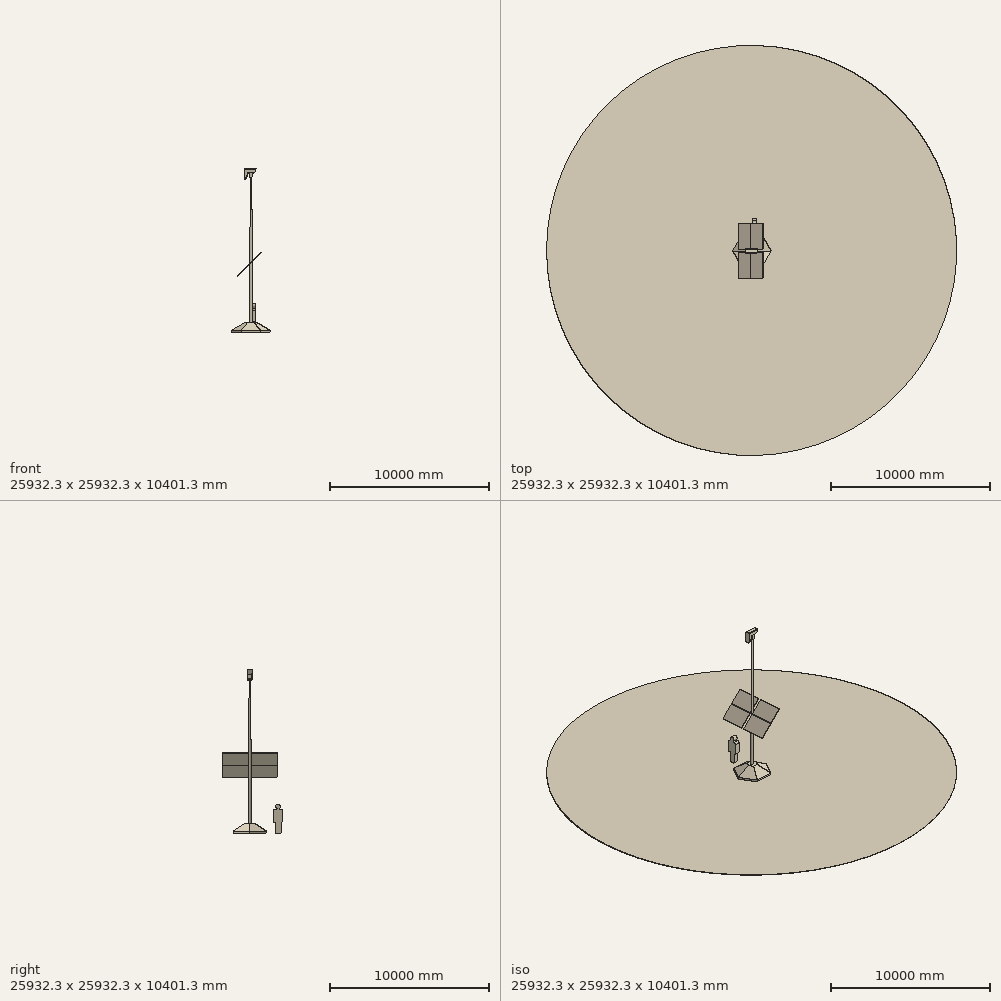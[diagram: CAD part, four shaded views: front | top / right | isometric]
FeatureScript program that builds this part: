
annotation { "Feature Type Name" : "Feature", "Feature Type Description" : "" }
export const myFeature = defineFeature(function(context is Context, id is Id, definition is map)
    precondition{}
    {
        {
            var Q0;
            Q0=qCreatedBy(makeId("Top.planeOp"),FACE);
            var sketch = newSketch(context, id + "F0", { "sketchPlane" : qUnion([Q0])});
            skCircle(sketch, "E0", {"center": v(0, 0) * mm, "radius": 101.6 * mm});
            skSolve(sketch);
        }
        {
            var Q0;
            Q0=qCreatedBy(makeId("Top.planeOp"),FACE);
            cPlane(context, id + "F1", {"entities" : qUnion([Q0]), "cplaneType" : CPlaneType.OFFSET, "offset" : 9144 * mm, "width" : 152.4 * mm, "height" : 152.4 * mm});
        }
        {
            var Q0;
            Q0=qCreatedBy(id+"F1.planeOp",FACE);
            var sketch = newSketch(context, id + "F2", { "sketchPlane" : qUnion([Q0])});
            skCircle(sketch, "E1", {"center": v(0, 0) * mm, "radius": 48.26 * mm});
            skSolve(sketch);
        }
        {
            var Q0;
            Q0=makeQuery(id+"F0.imprint","IMPRINT",FACE,{"disambiguationData":[TD([[makeQuery(id+"F0.imprint","IMPRINT",EDGE,{"derivedFrom":sQuery(id+"F0.wireOp",EDGE,"E0")}),1.0]])]});
            var Q1;
            Q1=makeQuery(id+"F2.imprint","IMPRINT",FACE,{"disambiguationData":[TD([[makeQuery(id+"F2.imprint","IMPRINT",EDGE,{"derivedFrom":sQuery(id+"F2.wireOp",EDGE,"E1")}),1.0]])]});
            loft(context, id + "F3", {"sheetProfilesArray" : [{ "sheetProfileEntities" : qUnion([Q0]) }, { "sheetProfileEntities" : qUnion([Q1]) }]});
        }
        {
            var Q0;
            Q0=qCreatedBy(makeId("Front.planeOp"),FACE);
            var sketch = newSketch(context, id + "F4", { "sketchPlane" : qUnion([Q0])});
            skLineSegment(sketch, "E2", {"start": v(703.54, 4411.94) * mm, "end": v(-50.8, 3657.6) * mm});
            skLineSegment(sketch, "E3", {"start": v(-50.8, 3657.6) * mm, "end": v(-86.72, 3693.52) * mm});
            skLineSegment(sketch, "E4", {"start": v(-86.72, 3693.52) * mm, "end": v(667.62, 4447.86) * mm});
            skLineSegment(sketch, "E5", {"start": v(667.62, 4447.86) * mm, "end": v(703.54, 4411.94) * mm});
            skLineSegment(sketch, "E6", {"start": v(-50.8, 3657.6) * mm, "end": v(703.54, 3657.6) * mm});
            skSolve(sketch);
        }
        {
            var Q0;
            Q0 = qSketchRegion(id + "F4", true);
            extrude(context, id + "F5", {"entities" : qUnion([Q0]), "depth" : 1752.6 * mm, "offsetDistance" : 25.4 * mm, "hasSecondDirection" : true, "secondDirectionOppositeDirection" : true, "secondDirectionDepth" : -101.6 * mm});
        }
        {
            var Q0;
            Q0=makeQuery(id+"F3.opLoft","CAP_FACE",FACE,{"disambiguationData":[OSD([makeQuery(id+"F2.imprint","IMPRINT",FACE,{"disambiguationData":[TD([[makeQuery(id+"F2.imprint","IMPRINT",EDGE,{"derivedFrom":sQuery(id+"F2.wireOp",EDGE,"E1")}),1.0]])]})])],"isStart":true});
            var Q1;
            Q1=makeQuery(id+"F3.opLoft","CAP_FACE",FACE,{"disambiguationData":[OSD([makeQuery(id+"F0.imprint","IMPRINT",FACE,{"disambiguationData":[TD([[makeQuery(id+"F0.imprint","IMPRINT",EDGE,{"derivedFrom":sQuery(id+"F0.wireOp",EDGE,"E0")}),1.0]])]})])],"isStart":true});
            shell(context, id + "F6", {"entities" : qUnion([Q0, Q1]), "thickness" : 4.13 * mm});
        }
        {
            var Q0;
            Q0=makeQuery(id+"F5.opExtrude","SWEPT_BODY",BODY,{"disambiguationData":[OSD([sQuery(id+"F4.wireOp",EDGE,"E2"),sQuery(id+"F4.wireOp",EDGE,"E3"),sQuery(id+"F4.wireOp",EDGE,"E4"),sQuery(id+"F4.wireOp",EDGE,"E5")])]});
            var Q1;
            Q1=qCreatedBy(makeId("Front.planeOp"),FACE);
            mirror(context, id + "F7", {"entities" : qUnion([Q0]), "mirrorPlane" : qUnion([Q1])});
        }
        {
            var Q0;
            Q0=makeQuery(id+"F5.opExtrude","SWEPT_FACE",FACE,{"disambiguationData":[OSD([sQuery(id+"F4.wireOp",EDGE,"E3")])]});
            cPlane(context, id + "F8", {"entities" : qUnion([Q0]), "cplaneType" : CPlaneType.OFFSET, "offset" : 12.7 * mm, "width" : 152.4 * mm, "height" : 152.4 * mm});
        }
        {
            var Q0;
            Q0=makeQuery(id+"F5.opExtrude","SWEPT_BODY",BODY,{"disambiguationData":[OSD([sQuery(id+"F4.wireOp",EDGE,"E2"),sQuery(id+"F4.wireOp",EDGE,"E3"),sQuery(id+"F4.wireOp",EDGE,"E4"),sQuery(id+"F4.wireOp",EDGE,"E5")])]});
            var Q1;
            Q1=makeQuery(id+"F7.opPattern","COPY",BODY,{"derivedFrom":makeQuery(id+"F5.opExtrude","SWEPT_BODY",BODY,{"disambiguationData":[OSD([sQuery(id+"F4.wireOp",EDGE,"E2"),sQuery(id+"F4.wireOp",EDGE,"E3"),sQuery(id+"F4.wireOp",EDGE,"E4"),sQuery(id+"F4.wireOp",EDGE,"E5")])]}),"instanceName":"1"});
            var Q2;
            Q2=qCreatedBy(id+"F8.planeOp",FACE);
            mirror(context, id + "F9", {"entities" : qUnion([Q0, Q1]), "mirrorPlane" : qUnion([Q2])});
        }
        {
            var Q0;
            Q0=makeQuery(id+"F3.opLoft","CAP_FACE",FACE,{"disambiguationData":[OSD([makeQuery(id+"F0.imprint","IMPRINT",FACE,{"disambiguationData":[TD([[makeQuery(id+"F0.imprint","IMPRINT",EDGE,{"derivedFrom":sQuery(id+"F0.wireOp",EDGE,"E0")}),1.0]])]})])],"isStart":true});
            var sketch = newSketch(context, id + "F10", { "sketchPlane" : qUnion([Q0])});
            skCircle(sketch, "E7.cCircle", {"center": v(0, 0) * mm, "radius": 1219.2 * mm, "construction": true});
            skLineSegment(sketch, "E7.0", {"start": v(1219.2, 0) * mm, "end": v(609.6, -1055.86) * mm});
            skLineSegment(sketch, "E7.1", {"start": v(609.6, -1055.86) * mm, "end": v(-609.6, -1055.86) * mm});
            skLineSegment(sketch, "E7.2", {"start": v(-609.6, -1055.86) * mm, "end": v(-1219.2, 0) * mm});
            skLineSegment(sketch, "E7.3", {"start": v(-1219.2, 0) * mm, "end": v(-609.6, 1055.86) * mm});
            skLineSegment(sketch, "E7.4", {"start": v(-609.6, 1055.86) * mm, "end": v(609.6, 1055.86) * mm});
            skLineSegment(sketch, "E7.5", {"start": v(609.6, 1055.86) * mm, "end": v(1219.2, 0) * mm});
            skSolve(sketch);
        }
        {
            var Q0;
            Q0 = qSketchRegion(id + "F10", true);
            extrude(context, id + "F11", {"entities" : qUnion([Q0]), "depth" : 635 * mm, "offsetDistance" : 25.4 * mm});
        }
        {
            var Q0;
            Q0=makeQuery(id+"F3.opLoft","CAP_FACE",FACE,{"disambiguationData":[OSD([makeQuery(id+"F2.imprint","IMPRINT",FACE,{"disambiguationData":[TD([[makeQuery(id+"F2.imprint","IMPRINT",EDGE,{"derivedFrom":sQuery(id+"F2.wireOp",EDGE,"E1")}),1.0]])]})])],"isStart":true});
            var sketch = newSketch(context, id + "F12", { "sketchPlane" : qUnion([Q0])});
            skLineSegment(sketch, "E8.bottom", {"start": v(76.2, 127) * mm, "end": v(-76.2, 127) * mm});
            skLineSegment(sketch, "E8.top", {"start": v(76.2, -127) * mm, "end": v(-76.2, -127) * mm});
            skLineSegment(sketch, "E8.left", {"start": v(76.2, 127) * mm, "end": v(76.2, -127) * mm});
            skLineSegment(sketch, "E8.right", {"start": v(-76.2, 127) * mm, "end": v(-76.2, -127) * mm});
            skPoint(sketch, "E8.middle", {"position": v(0, 0) * mm});
            skSolve(sketch);
        }
        {
            var Q0;
            Q0 = qSketchRegion(id + "F12", true);
            extrude(context, id + "F13", {"entities" : qUnion([Q0]), "operationType" : NewBodyOperationType.ADD, "depth" : 292.1 * mm, "offsetDistance" : 25.4 * mm});
        }
        {
            var Q0;
            Q0=qCreatedBy(makeId("Front.planeOp"),FACE);
            var sketch = newSketch(context, id + "F14", { "sketchPlane" : qUnion([Q0])});
            skLineSegment(sketch, "E9.0", {"start": v(76.2, 9436.1) * mm, "end": v(-76.2, 9436.1) * mm});
            skLineSegment(sketch, "E10", {"start": v(76.2, 9436.1) * mm, "end": v(228.6, 9436.1) * mm});
            skLineSegment(sketch, "E11", {"start": v(228.6, 9436.1) * mm, "end": v(348.34, 9740.9) * mm});
            skLineSegment(sketch, "E12", {"start": v(348.34, 9740.9) * mm, "end": v(-413.66, 9740.9) * mm});
            skLineSegment(sketch, "E13", {"start": v(-413.66, 9740.9) * mm, "end": v(-413.66, 9029.7) * mm});
            skLineSegment(sketch, "E14", {"start": v(-413.66, 9029.7) * mm, "end": v(-312.06, 9029.7) * mm});
            skLineSegment(sketch, "E15", {"start": v(-312.06, 9029.7) * mm, "end": v(-152.4, 9436.1) * mm});
            skLineSegment(sketch, "E16", {"start": v(-152.4, 9436.1) * mm, "end": v(-76.2, 9436.1) * mm});
            skSolve(sketch);
        }
        {
            var Q0;
            Q0 = qSketchRegion(id + "F14", true);
            extrude(context, id + "F15", {"entities" : qUnion([Q0]), "operationType" : NewBodyOperationType.ADD, "endBound" : BoundingType.SYMMETRIC, "depth" : 304.8 * mm, "offsetDistance" : 25.4 * mm});
        }
        {
            var Q0;
            Q0=makeQuery(id+"F15.opExtrude","CAP_EDGE",EDGE,{"disambiguationData":[OSD([sQuery(id+"F14.wireOp",EDGE,"E12")])],"isStart":false});
            var Q1;
            Q1=makeQuery(id+"F15.opExtrude","CAP_EDGE",EDGE,{"disambiguationData":[OSD([sQuery(id+"F14.wireOp",EDGE,"E12")])],"isStart":true});
            var Q2;
            Q2=makeQuery(id+"F15.opExtrude","CAP_EDGE",EDGE,{"disambiguationData":[OSD([sQuery(id+"F14.wireOp",EDGE,"E9.0"),sQuery(id+"F14.wireOp",EDGE,"E10"),sQuery(id+"F14.wireOp",EDGE,"E16")])],"isStart":false});
            var Q3;
            Q3=makeQuery(id+"F15.opExtrude","CAP_EDGE",EDGE,{"disambiguationData":[OSD([sQuery(id+"F14.wireOp",EDGE,"E14")])],"isStart":false});
            var Q4;
            Q4=makeQuery(id+"F15.opExtrude","CAP_EDGE",EDGE,{"disambiguationData":[OSD([sQuery(id+"F14.wireOp",EDGE,"E15")])],"isStart":false});
            var Q5;
            Q5=makeQuery(id+"F15.opExtrude","SWEPT_EDGE",EDGE,{"disambiguationData":[OSD([sQuery(id+"F14.wireOp",EDGE,"E15"),sQuery(id+"F14.wireOp",EDGE,"E16")])]});
            var Q6;
            Q6=makeQuery(id+"F15.opExtrude","SWEPT_EDGE",EDGE,{"disambiguationData":[OSD([sQuery(id+"F14.wireOp",EDGE,"E14"),sQuery(id+"F14.wireOp",EDGE,"E15")])]});
            var Q7;
            Q7=makeQuery(id+"F15.opExtrude","CAP_EDGE",EDGE,{"disambiguationData":[OSD([sQuery(id+"F14.wireOp",EDGE,"E14")])],"isStart":true});
            var Q8;
            Q8=makeQuery(id+"F15.opExtrude","CAP_EDGE",EDGE,{"disambiguationData":[OSD([sQuery(id+"F14.wireOp",EDGE,"E15")])],"isStart":true});
            var Q9;
            Q9=makeQuery(id+"F15.opExtrude","CAP_EDGE",EDGE,{"disambiguationData":[OSD([sQuery(id+"F14.wireOp",EDGE,"E9.0"),sQuery(id+"F14.wireOp",EDGE,"E10"),sQuery(id+"F14.wireOp",EDGE,"E16")])],"isStart":true});
            fillet(context, id + "F16", {"entities" : qUnion([Q0, Q1, Q2, Q3, Q4, Q5, Q6, Q7, Q8, Q9]), "radius" : 50.8 * mm, "tangentPropagation" : true, "allowEdgeOverflow" : false});
        }
        {
            var Q0;
            Q0=makeQuery(id+"F11.opExtrude","CAP_EDGE",EDGE,{"disambiguationData":[OSD([sQuery(id+"F10.wireOp",EDGE,"E7.2")])],"isStart":true});
            var Q1;
            Q1=makeQuery(id+"F11.opExtrude","CAP_EDGE",EDGE,{"disambiguationData":[OSD([sQuery(id+"F10.wireOp",EDGE,"E7.3")])],"isStart":true});
            var Q2;
            Q2=makeQuery(id+"F11.opExtrude","CAP_EDGE",EDGE,{"disambiguationData":[OSD([sQuery(id+"F10.wireOp",EDGE,"E7.4")])],"isStart":true});
            var Q3;
            Q3=makeQuery(id+"F11.opExtrude","CAP_EDGE",EDGE,{"disambiguationData":[OSD([sQuery(id+"F10.wireOp",EDGE,"E7.5")])],"isStart":true});
            var Q4;
            Q4=makeQuery(id+"F11.opExtrude","CAP_EDGE",EDGE,{"disambiguationData":[OSD([sQuery(id+"F10.wireOp",EDGE,"E7.0")])],"isStart":true});
            var Q5;
            Q5=makeQuery(id+"F11.opExtrude","CAP_EDGE",EDGE,{"disambiguationData":[OSD([sQuery(id+"F10.wireOp",EDGE,"E7.1")])],"isStart":true});
            chamfer(context, id + "F17", {"entities" : qUnion([Q0, Q1, Q2, Q3, Q4, Q5]), "chamferType" : ChamferType.TWO_OFFSETS, "width1" : 762 * mm, "oppositeDirection" : false, "width2" : 508 * mm, "tangentPropagation" : true});
        }
        {
            var Q0;
            Q0=makeQuery(id+"F15.opExtrude","SWEPT_FACE",FACE,{"disambiguationData":[OSD([sQuery(id+"F14.wireOp",EDGE,"E13")])]});
            var sketch = newSketch(context, id + "F18", { "sketchPlane" : qUnion([Q0])});
            skLineSegment(sketch, "E17.0.0", {"start": v(101.6, 9740.9) * mm, "end": v(-101.6, 9740.9) * mm});
            skArc(sketch, "E17.0.1", {"start": v(-101.6, 9740.9) * mm, "mid": v(-137.52, 9726.02) * mm, "end": v(-152.4, 9690.1) * mm});
            skLineSegment(sketch, "E17.0.2", {"start": v(-152.4, 9690.1) * mm, "end": v(-152.4, 9080.5) * mm});
            skArc(sketch, "E17.0.3", {"start": v(-152.4, 9080.5) * mm, "mid": v(-137.52, 9044.58) * mm, "end": v(-101.6, 9029.7) * mm});
            skLineSegment(sketch, "E17.0.4", {"start": v(-101.6, 9029.7) * mm, "end": v(101.6, 9029.7) * mm});
            skArc(sketch, "E17.0.5", {"start": v(101.6, 9029.7) * mm, "mid": v(137.52, 9044.58) * mm, "end": v(152.4, 9080.5) * mm});
            skLineSegment(sketch, "E17.0.6", {"start": v(152.4, 9080.5) * mm, "end": v(152.4, 9690.1) * mm});
            skArc(sketch, "E17.0.7", {"start": v(152.4, 9690.1) * mm, "mid": v(137.52, 9726.02) * mm, "end": v(101.6, 9740.9) * mm});
            skSolve(sketch);
        }
        {
            var Q0;
            Q0 = qSketchRegion(id + "F18", true);
            extrude(context, id + "F19", {"entities" : qUnion([Q0]), "depth" : 5.08 * mm, "offsetDistance" : 25.4 * mm});
        }
        {
            var Q0;
            Q0=makeQuery(id+"F11.opExtrude","CAP_FACE",FACE,{"disambiguationData":[OSD([sQuery(id+"F10.wireOp",EDGE,"E7.0"),sQuery(id+"F10.wireOp",EDGE,"E7.1"),sQuery(id+"F10.wireOp",EDGE,"E7.2"),sQuery(id+"F10.wireOp",EDGE,"E7.3"),sQuery(id+"F10.wireOp",EDGE,"E7.4"),sQuery(id+"F10.wireOp",EDGE,"E7.5")])],"isStart":false});
            var sketch = newSketch(context, id + "F20", { "sketchPlane" : qUnion([Q0])});
            skCircle(sketch, "E18", {"center": v(-26.8, -39.26) * mm, "radius": 12966.17 * mm});
            skSolve(sketch);
        }
        {
            var Q0;
            Q0 = qSketchRegion(id + "F20", true);
            extrude(context, id + "F21", {"entities" : qUnion([Q0]), "depth" : 25.4 * mm, "offsetDistance" : 25.4 * mm});
        }
        {
            var Q0;
            Q0=qCreatedBy(makeId("Right.planeOp"),FACE);
            var sketch = newSketch(context, id + "F22", { "sketchPlane" : qUnion([Q0])});
            skArc(sketch, "E19", {"start": v(1836.6, 897.22) * mm, "mid": v(1787.23, 1193.8) * mm, "end": v(1737.87, 897.22) * mm});
            skLineSegment(sketch, "E20.bottom", {"start": v(1965.03, 897.22) * mm, "end": v(1836.6, 897.22) * mm});
            skLineSegment(sketch, "E20.top", {"start": v(1980.38, -628.36) * mm, "end": v(1624.88, -628.36) * mm});
            skLineSegment(sketch, "E20.left", {"start": v(2092.03, 770.22) * mm, "end": v(2092.03, 67.24) * mm});
            skLineSegment(sketch, "E20.right", {"start": v(1482.43, 770.22) * mm, "end": v(1482.43, 61.65) * mm});
            skLineSegment(sketch, "E21.trimOffspring", {"start": v(1737.87, 897.22) * mm, "end": v(1609.43, 897.22) * mm});
            skPoint(sketch, "E22.visualSharp", {"position": v(2092.03, 897.22) * mm});
            skArc(sketch, "E22.filletArc", {"start": v(2092.03, 770.22) * mm, "mid": v(2054.83, 860.02) * mm, "end": v(1965.03, 897.22) * mm});
            skPoint(sketch, "E23.visualSharp", {"position": v(1482.43, 897.22) * mm});
            skArc(sketch, "E23.filletArc", {"start": v(1609.43, 897.22) * mm, "mid": v(1519.63, 860.02) * mm, "end": v(1482.43, 770.22) * mm});
            skLineSegment(sketch, "E24.top", {"start": v(2092.03, 67.24) * mm, "end": v(1980.38, 67.24) * mm});
            skLineSegment(sketch, "E24.right", {"start": v(1980.38, -628.36) * mm, "end": v(1980.38, 67.24) * mm});
            skLineSegment(sketch, "E25.top", {"start": v(1482.43, 61.65) * mm, "end": v(1624.88, 61.65) * mm});
            skLineSegment(sketch, "E25.right", {"start": v(1624.88, -628.36) * mm, "end": v(1624.88, 61.65) * mm});
            skSolve(sketch);
        }
        {
            var Q0;
            Q0 = qSketchRegion(id + "F22", true);
            extrude(context, id + "F23", {"entities" : qUnion([Q0]), "depth" : 304.8 * mm, "offsetDistance" : 25.4 * mm});
        }
    });
